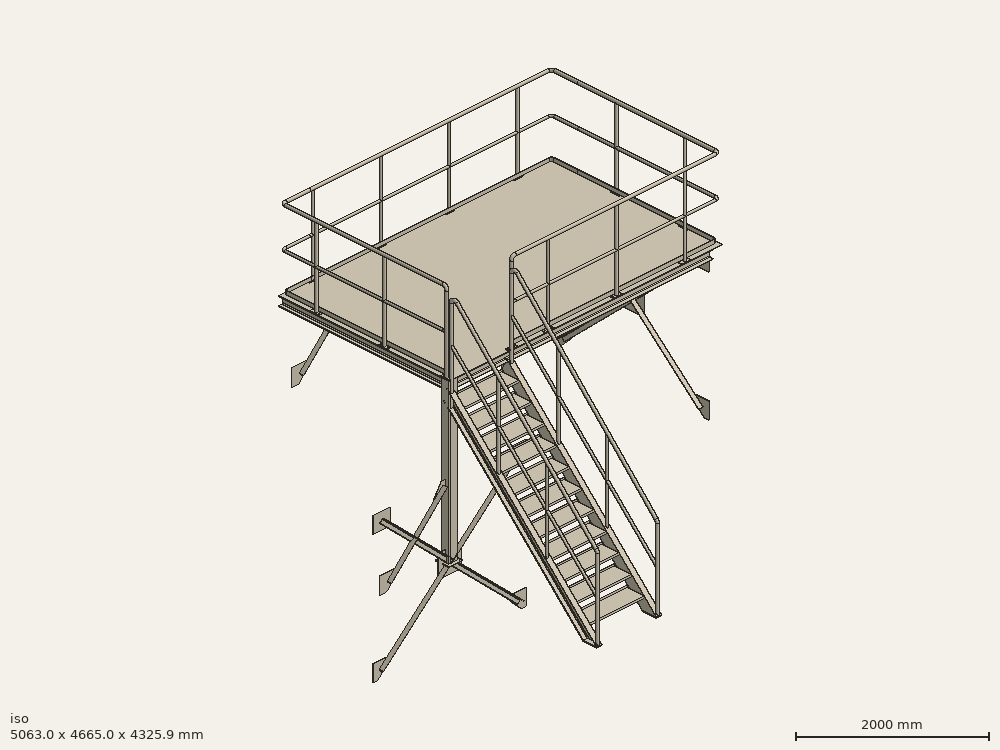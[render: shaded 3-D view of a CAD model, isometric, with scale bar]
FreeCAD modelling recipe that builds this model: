
FCSTD DOCUMENT  (FreeCAD 0.21R33668 +26 (Git))
Label: STBsample
License: All rights reserved
LicenseURL: http://en.wikipedia.org/wiki/All_rights_reserved
objects: Part::FeaturePython×14, Part::Mirroring×6, Part::Extrusion×5, Sketcher::SketchObject×4, Part::MultiFuse×3, Spreadsheet::Sheet×3, App::Part×3, Part::Cut×1
note: 30 computed .brp shape members not serialized (recipe doc carries the construction recipe); baked Part::Feature solids carry a one-line shape summary decoded from their .brp

FEATURE [Part::FeaturePython] BasePlate  # WARN: FeaturePython — macro-defined, semantics opaque (R4)
  B = 200
  D = 15
  H = 200
  b1 = 20
  h1 = 20
  sface = 0
FEATURE [Part::Extrusion] Extrude002  label="Extrude"
  Base = -> BasePlate
  Dir = (0,0,1)
  DirMode = 2
  FaceMakerClass = Part::FaceMakerBullseye
  LengthFwd = 10
  LengthRev = 0
  Solid = true
  Symmetric = false
FEATURE [Part::FeaturePython] Square_Pipe  # WARN: FeaturePython — macro-defined, semantics opaque (R4)
  A = 125
  H = 125
  L = 2200
  Solid = true
  g0 = 7.85
  mass = 47.7221
  size = 40
  standard = SS
  expr: L = Spreadsheet001.H0
FEATURE [Part::MultiFuse] Fusion002  label="PostSq"
  Shapes = -> [Extrude002,Square_Pipe]
FEATURE [Part::FeaturePython] Array  label="post"  # Draft array (typed FeaturePython)
  AlwaysSyncPlacement = false
  Angle = 360
  ArrayType = 0
  Axis = (0,0,1)
  Base = -> Fusion002
  Center = (0,0,0)
  Count = 4
  ExpandArray = false
  Fuse = false
  IntervalAxis = (0,0,0)
  IntervalX = (3875,0,0)
  IntervalY = (0,2375,0)
  IntervalZ = (0,0,2200)
  NumberCircles = 3
  NumberPolar = 5
  NumberX = 2
  NumberY = 2
  NumberZ = 1
  PlacementList = 4 placements: [(0,0,0),(0,2375,0),(3875,0,0),(3875,2375,0)]
  RadialDistance = 50
  ScaleList = (4) [(1,1,1),(1,1,1),(1,1,1),(1,1,1)]
  Symmetry = 1
  TangentialDistance = 25
  expr: .IntervalX.x = Spreadsheet001.W0 - 125
  expr: .IntervalY.y = Spreadsheet001.L0 - 125
FEATURE [Part::FeaturePython] HShapeSteel  # WARN: FeaturePython — macro-defined, semantics opaque (R4)
  B = 125
  H = 125
  L = 2375
  Placement = pos=(0,62.5,2137.5) rot=(-1,0,0;1.5708rad)
  Solid = true
  g0 = 7.85
  mass = 56.5156
  size = 1
  standard = SS_Wide
  t1 = 6.5
  t2 = 9
  expr: .Placement.Base.z = Spreadsheet001.H0 - 62.5
  expr: L = Spreadsheet001.L0 - 125
FEATURE [Part::FeaturePython] Array001  label="beam_v"  # Draft array (typed FeaturePython)
  AlwaysSyncPlacement = false
  Angle = 360
  ArrayType = 0
  Axis = (0,0,1)
  Base = -> HShapeSteel
  Center = (0,0,0)
  Count = 2
  ExpandArray = false
  Fuse = false
  IntervalAxis = (0,0,0)
  IntervalX = (3875,0,0)
  IntervalY = (0,100,0)
  IntervalZ = (0,0,100)
  NumberCircles = 3
  NumberPolar = 5
  NumberX = 2
  NumberY = 1
  NumberZ = 1
  PlacementList = 2 placements: [(0,62.5,2137.5),(3875,62.5,2137.5)]
  RadialDistance = 50
  ScaleList = (2) [(1,1,1),(1,1,1)]
  Symmetry = 1
  TangentialDistance = 25
  expr: .IntervalX.x = Spreadsheet001.W0 - 125
FEATURE [Part::FeaturePython] HShapeSteel001  # WARN: FeaturePython — macro-defined, semantics opaque (R4)
  B = 125
  H = 125
  L = 3750
  Placement = pos=(62.5,0,2137.5) rot=(0.57735,-0.57735,0.57735;4.18879rad)
  Solid = true
  g0 = 7.85
  mass = 89.2351
  size = 1
  standard = SS_Wide
  t1 = 6.5
  t2 = 9
  expr: .Placement.Base.z = Spreadsheet001.H0 - 62.5
  expr: L = Spreadsheet001.W0 - 125 * 2
FEATURE [Part::FeaturePython] Array002  label="beam_h"  # Draft array (typed FeaturePython)
  AlwaysSyncPlacement = false
  Angle = 360
  ArrayType = 0
  Axis = (0,0,1)
  Base = -> HShapeSteel001
  Center = (0,0,0)
  Count = 2
  ExpandArray = false
  Fuse = false
  IntervalAxis = (0,0,0)
  IntervalX = (100,0,0)
  IntervalY = (0,2375,0)
  IntervalZ = (0,0,100)
  NumberCircles = 3
  NumberPolar = 5
  NumberX = 1
  NumberY = 2
  NumberZ = 1
  PlacementList = 2 placements: [(62.5,0,2137.5),(62.5,2375,2137.5)]
  RadialDistance = 50
  ScaleList = (2) [(1,1,1),(1,1,1)]
  Symmetry = 1
  TangentialDistance = 25
  expr: .IntervalY.y = Spreadsheet001.L0 - 125
FEATURE [Spreadsheet::Sheet] Spreadsheet001  label="Spreadsheet"
  cells = A2='W; B2(W0)=4000; A3='L; B3(L0)=2500; A4='H; B4(H0)=2200
FEATURE [Sketcher::SketchObject] Sketch002
  FullyConstrained = true
  expr: Constraints[8] = Spreadsheet001.L0
  expr: Constraints[9] = Spreadsheet001.W0
  sketch-geometry (4):
    g0: LineSegment StartX=-62.5 StartY=-62.5 StartZ=0 EndX=3937.5 EndY=-62.5 EndZ=0
    g1: LineSegment StartX=3937.5 StartY=-62.5 StartZ=0 EndX=3937.5 EndY=2437.5 EndZ=0
    g2: LineSegment StartX=3937.5 StartY=2437.5 StartZ=0 EndX=-62.5 EndY=2437.5 EndZ=0
    g3: LineSegment StartX=-62.5 StartY=2437.5 StartZ=0 EndX=-62.5 EndY=-62.5 EndZ=0
  constraints (12):
    c: Coincident(g0,g1)
    c: Coincident(g1,g2)
    c: Coincident(g2,g3)
    c: Coincident(g3,g0)
    c: Horizontal(g0)
    c: Horizontal(g2)
    c: Vertical(g1)
    c: Vertical(g3)
    c: DistanceY(g3,g3) = 2500
    c: DistanceX(g2,g2) = 4000
    c: DistanceY(g0,g-1) = 62.5
    c: DistanceX(g0,g-1) = 62.5
FEATURE [Part::Extrusion] Extrude003  label="chpl"
  Base = -> Sketch002
  Dir = (0,0,1)
  DirMode = 2
  FaceMakerClass = Part::FaceMakerBullseye
  LengthFwd = 4.5
  LengthRev = 0
  Placement = pos=(0,0,2200) rot=(0,0,1;0rad)
  Solid = true
  Symmetric = false
  expr: .Placement.Base.z = Spreadsheet001.H0
FEATURE [Part::FeaturePython] Corner001  # WARN: FeaturePython — macro-defined, semantics opaque (R4)
  Placement = pos=(363,2413,2204.5) rot=(0,0,1;0rad)
  Reverse = true
  g0 = 7.85
  h = 1100
  k = -90
  l1 = 3550
  l2 = 400
  mass = 43.6699
  p = 1000
  spec = 0
  type = 2
  expr: .Placement.Base.y = Spreadsheet001.L0 - 87
  expr: .Placement.Base.z = Spreadsheet001.H0 + 4.5
  expr: l1 = Spreadsheet001.W0 - 450
FEATURE [Part::FeaturePython] Corner_with_end001  # WARN: FeaturePython — macro-defined, semantics opaque (R4)
  Placement = pos=(877,-37,2204.5) rot=(0,0,1;0rad)
  Reverse = false
  g0 = 7.85
  h = 1100
  k = 90
  l1 = 3036
  l2 = 2050
  mass = 59.9755
  p = 1000
  spec = 0
  type = 1
  expr: .Placement.Base.z = Spreadsheet001.H0 + 4.5
  expr: l1 = Spreadsheet001.W0 - 1000 + 36
  expr: l2 = Spreadsheet001.L0 - 450
FEATURE [Part::FeaturePython] SteelStair  # WARN: FeaturePython — macro-defined, semantics opaque (R4)
  H = 2200
  HighPlace = false
  L = 2200
  L1 = 70
  Placement = pos=(12,-2227,-101.5) rot=(0,0,1;1.5708rad)
  Position = 2
  body = 172.99
  handrail = 57.5144
  mass = 230.504
  size = 1
  t = 9
  type = 1
  w = 800
  expr: .Placement.Base.y = -Spreadsheet001.H0 - 27
FEATURE [Part::FeaturePython] Corner_with_end  # WARN: FeaturePython — macro-defined, semantics opaque (R4)
  Placement = pos=(-36,-8e-15,2204.5) rot=(0,0,1;1.5708rad)
  Reverse = true
  g0 = 7.85
  h = 1100
  k = -90
  l1 = 2413
  l2 = 400
  mass = 32.6673
  p = 1000
  spec = 0
  type = 1
  expr: .Placement.Base.z = Spreadsheet001.H0 + 4.5
  expr: l1 = Spreadsheet001.L0 - 100 + 13
FEATURE [App::Part] Part001  label="Trstle"
  Group = -> [HShapeSteel001,Array002,HShapeSteel,Array001,Fusion002,Square_Pipe,BasePlate,Extrude002,Array,Spreadsheet001,Sketch002,Extrude003,Corner001,Corner_with_end001,SteelStair,Corner_with_end]
  Origin = -> Origin001
FEATURE [Sketcher::SketchObject] Sketch
  FullyConstrained = true
  MapMode = 5
  Placement = pos=(0,0,0) rot=(1,0,0;1.5708rad)
  expr: Constraints[10] = Spreadsheet.H0
  expr: Constraints[11] = Spreadsheet.W0
  expr: Constraints[27] = Spreadsheet.La
  expr: Constraints[28] = Spreadsheet.B0 + 10
  expr: Constraints[37] = Spreadsheet.La
  expr: Constraints[38] = Spreadsheet.B0 + 10
  expr: Constraints[56] = Spreadsheet.B0 + 10
  expr: Constraints[57] = Spreadsheet.La
  expr: Constraints[59] = Spreadsheet.B0 + 10
  expr: Constraints[61] = Spreadsheet.La
  sketch-geometry (36):
    g0: LineSegment StartX=-1125 StartY=-1000 StartZ=0 EndX=-1125 EndY=1000 EndZ=0
    g1: LineSegment StartX=-1125 StartY=1000 StartZ=0 EndX=1125 EndY=1000 EndZ=0
    g2: LineSegment StartX=1125 StartY=1000 StartZ=0 EndX=1125 EndY=-1000 EndZ=0
    g3: LineSegment StartX=1125 StartY=-1000 StartZ=0 EndX=-1125 EndY=-1000 EndZ=0
    g4: GeomPoint X=0 Y=0 Z=0
    g5: LineSegment StartX=-1125 StartY=-1000 StartZ=0 EndX=1125 EndY=1000 EndZ=0
    g6: LineSegment StartX=-1125 StartY=1000 StartZ=0 EndX=1125 EndY=-1000 EndZ=0
    g7: LineSegment StartX=-1125 StartY=1000 StartZ=0 EndX=-875.864 EndY=1000 EndZ=0
    g8: LineSegment StartX=-875.864 StartY=1000 StartZ=0 EndX=-875.864 EndY=828.719 EndZ=0
    g9: LineSegment StartX=-875.864 StartY=828.719 StartZ=0 EndX=-925.691 EndY=772.663 EndZ=0
    g10: LineSegment StartX=-925.691 StartY=772.663 StartZ=0 EndX=-1125 EndY=772.663 EndZ=0
    g11: LineSegment StartX=-1125 StartY=772.663 StartZ=0 EndX=-1125 EndY=1000 EndZ=0
    g12: LineSegment StartX=-1125 StartY=-1000 StartZ=0 EndX=-1050 EndY=-1000 EndZ=0
    g13: LineSegment StartX=-925.691 StartY=-772.663 StartZ=0 EndX=-1125 EndY=-772.663 EndZ=0
    g14: LineSegment StartX=-1125 StartY=-772.663 StartZ=0 EndX=-1125 EndY=-1000 EndZ=0
    g15: LineSegment StartX=-875.864 StartY=-828.719 StartZ=0 EndX=-925.691 EndY=-772.663 EndZ=0
    g16: LineSegment StartX=1125 StartY=1000 StartZ=0 EndX=875.864 EndY=1000 EndZ=0
    g17: LineSegment StartX=875.864 StartY=1000 StartZ=0 EndX=875.864 EndY=828.719 EndZ=0
    g18: LineSegment StartX=925.691 StartY=772.663 StartZ=0 EndX=1125 EndY=772.663 EndZ=0
    g19: LineSegment StartX=1125 StartY=772.663 StartZ=0 EndX=1125 EndY=1000 EndZ=0
    g20: LineSegment StartX=1125 StartY=-1000 StartZ=0 EndX=1050 EndY=-1000 EndZ=0
    g21: LineSegment StartX=925.691 StartY=-772.663 StartZ=0 EndX=1125 EndY=-772.663 EndZ=0
    g22: LineSegment StartX=1125 StartY=-772.663 StartZ=0 EndX=1125 EndY=-1000 EndZ=0
    g23: LineSegment StartX=925.691 StartY=772.663 StartZ=0 EndX=875.864 EndY=828.719 EndZ=0
    g24: LineSegment StartX=875.864 StartY=-828.719 StartZ=0 EndX=925.691 EndY=-772.663 EndZ=0
    g25: LineSegment StartX=-171.074 StartY=-108.582 StartZ=0 EndX=-171.074 EndY=108.582 EndZ=0
    g26: LineSegment StartX=-127.89 StartY=157.164 StartZ=0 EndX=127.89 EndY=157.164 EndZ=0
    g27: LineSegment StartX=171.074 StartY=108.582 StartZ=0 EndX=171.074 EndY=-108.582 EndZ=0
    g28: LineSegment StartX=127.89 StartY=-157.164 StartZ=0 EndX=-127.89 EndY=-157.164 EndZ=0
    g29: GeomPoint X=0 Y=0 Z=0
    g30: LineSegment StartX=171.074 StartY=108.582 StartZ=0 EndX=127.89 EndY=157.164 EndZ=0
    g31: LineSegment StartX=-127.89 StartY=157.164 StartZ=0 EndX=-171.074 EndY=108.582 EndZ=0
    g32: LineSegment StartX=-127.89 StartY=-157.164 StartZ=0 EndX=-171.074 EndY=-108.582 EndZ=0
    g33: LineSegment StartX=127.89 StartY=-157.164 StartZ=0 EndX=171.074 EndY=-108.582 EndZ=0
    g34: LineSegment StartX=-875.864 StartY=-828.719 StartZ=0 EndX=-1050 EndY=-1000 EndZ=0
    g35: LineSegment StartX=875.864 StartY=-828.719 StartZ=0 EndX=1050 EndY=-1000 EndZ=0
  constraints (90):
    c: Coincident(g0,g1)
    c: Coincident(g1,g2)
    c: Coincident(g2,g3)
    c: Coincident(g3,g0)
    c: Horizontal(g1)
    c: Horizontal(g3)
    c: Vertical(g0)
    c: Vertical(g2)
    c: Symmetric(g1,g0,g4)
    c: Coincident(g4,g-1)
    c: DistanceY(g2,g2) = 2000
    c: DistanceX(g1,g1) = 2250
    c: Coincident(g5,g0)
    c: Coincident(g5,g1)
    c: Coincident(g6,g0)
    c: Coincident(g6,g2)
    c: Coincident(g0,g7)
    c: PointOnObject(g7,g1)
    c: Coincident(g7,g8)
    c: Vertical(g8)
    c: Coincident(g8,g9)
    c: Coincident(g9,g10)
    c: PointOnObject(g10,g0)
    c: Horizontal(g10)
    c: Coincident(g10,g11)
    c: Coincident(g11,g7)
    c: Symmetric(g8,g9,g6)
    c: Distance(g7,g9) = 300
    c: Distance(g9) = 75
    c: Coincident(g13,g14)
    c: Coincident(g14,g12)
    c: Horizontal(g12)
    c: Horizontal(g13)
    c: Vertical(g14)
    c: Coincident(g12,g0)
    c: Coincident(g13,g15)
    c: Symmetric(g15,g13,g5)
    c: Distance(g12,g15) = 300
    c: Distance(g15) = 75
    c: Coincident(g16,g17)
    c: Coincident(g18,g19)
    c: Coincident(g19,g16)
    c: Horizontal(g16)
    c: Horizontal(g18)
    c: Vertical(g17)
    c: Vertical(g19)
    c: Coincident(g16,g1)
    c: Coincident(g21,g22)
    c: Coincident(g22,g20)
    c: Horizontal(g20)
    c: Horizontal(g21)
    c: Vertical(g22)
    c: Coincident(g20,g2)
    c: Coincident(g18,g23)
    c: Coincident(g17,g23)
    c: Symmetric(g18,g17,g5)
    c: Distance(g23) = 75
    c: Distance(g16,g23) = 300
    c: Coincident(g21,g24)
    c: Distance(g24) = 75
    c: Symmetric(g21,g24,g6)
    c: Distance(g20,g24) = 300
    c: Horizontal(g26)
    c: Horizontal(g28)
    c: Vertical(g25)
    c: Vertical(g27)
    c: Coincident(g29,g4)
    c: Coincident(g27,g30)
    c: Coincident(g26,g30)
    c: Coincident(g26,g31)
    c: Coincident(g25,g31)
    c: Coincident(g25,g32)
    c: Coincident(g28,g32)
    c: Coincident(g28,g33)
    c: Coincident(g27,g33)
    c: Perpendicular(g5,g32)
    c: Distance(g31) = 65
    c: Symmetric(g26,g25,g6)
    c: Equal(g31,g30)
    c: Equal(g33,g31)
    c: Equal(g31,g32)
    c: Symmetric(g27,g26,g5)
    c: Symmetric(g27,g28,g6)
    c: Distance(g4,g30) = 200
    c: Coincident(g12,g34)
    c: DistanceX(g12,g12) = 75
    c: Coincident(g34,g15)
    c: Coincident(g20,g35)
    c: DistanceX(g20,g20) = 75
    c: Coincident(g35,g24)
FEATURE [Part::Extrusion] Extrude  label="GPL"
  Base = -> Sketch
  Dir = (0,-1,2e-16)
  DirMode = 2
  FaceMakerClass = Part::FaceMakerBullseye
  LengthFwd = 6
  LengthRev = 0
  Solid = true
  Symmetric = false
FEATURE [Spreadsheet::Sheet] Spreadsheet  label="STB02"
  cells = A2='ブレース幅W0; B2(W0)=2250; A3='ブレース高H0; B3(H0)=2000; A4='ブレース長C0; B4(C0)==sqrt(W0 ^ 2 + H0 ^ 2); A5='ガセットプレートLa; B5(La)=300; A6='ブレース角度k0; B6(k0)==atan(H0 / W0); A7='ブレース部材幅B0; B7(B0)=65
FEATURE [Part::FeaturePython] AngleSteel  # WARN: FeaturePython — macro-defined, semantics opaque (R4)
  A = 65
  B = 65
  L = 1355.2
  Placement = pos=(0,-38.5,0) rot=(0,1,0;2.29744rad)
  Solid = true
  g0 = 7.85
  mass = 8.0068
  sface = 0
  size = 8
  standard = SS_Equal
  t = 6
  expr: .Placement.Rotation.Angle = Spreadsheet.k0 + 90 °
  expr: L = Spreadsheet.C0 / 2 - Spreadsheet.La + 150
FEATURE [Part::Mirroring] Part__Mirroring001  label="AngleSteel (Mirror #2)"
  Base = (0,0,0)
  Normal = (1,0,0)
  Placement = pos=(0,-8,0) rot=(0,1,0;1.45328rad)
  Source = -> AngleSteel
  expr: .Placement.Rotation.Angle = Spreadsheet.k0 * 2
FEATURE [Part::FeaturePython] AngleSteel001  # WARN: FeaturePython — macro-defined, semantics opaque (R4)
  A = 65
  B = 65
  L = 1355.2
  Placement = pos=(0,-38.5,0) rot=(0,1,0;0.844154rad)
  Solid = true
  g0 = 7.85
  mass = 8.0068
  sface = 1
  size = 8
  standard = SS_Equal
  t = 6
  expr: .Placement.Rotation.Angle = 90 ° - Spreadsheet.k0
  expr: L = Spreadsheet.C0 / 2 - Spreadsheet.La + 150
FEATURE [Part::Mirroring] Part__Mirroring  label="AngleSteel001 (Mirror #2)"
  Base = (0,0,0)
  Normal = (0,0,1)
  Placement = pos=(0,0,0) rot=(0,1,0;1.68831rad)
  Source = -> AngleSteel001
  expr: .Placement.Rotation.Angle = (90 ° - Spreadsheet.k0) * 2
FEATURE [Part::MultiFuse] Fusion  label="beam_b"
  Refine = true
  Shapes = -> [Part__Mirroring001,AngleSteel]
FEATURE [Part::MultiFuse] Fusion001  label="beamA"
  Shapes = -> [Part__Mirroring,AngleSteel001]
FEATURE [Sketcher::SketchObject] Sketch001
  ExternalGeometry = -> [Extrude,Fusion001,Fusion]
  FullyConstrained = true
  MapMode = 5
  Placement = pos=(0,-6,1.3e-15) rot=(1,0,0;1.5708rad)
  Support = -> [Extrude]
  sketch-geometry (4):
    g0: LineSegment StartX=0 StartY=69.5737 StartZ=0 EndX=-78.2704 EndY=0 EndZ=0
    g1: LineSegment StartX=-78.2704 StartY=0 StartZ=0 EndX=-2.84e-14 EndY=-69.5737 EndZ=0
    g2: LineSegment StartX=-3.11e-14 StartY=-69.5737 StartZ=0 EndX=78.2704 EndY=0 EndZ=0
    g3: LineSegment StartX=78.2704 StartY=0 StartZ=0 EndX=0 EndY=69.5737 EndZ=0
  constraints (12):
    c: PointOnObject(g0,g-2)
    c: PointOnObject(g0,g-1)
    c: Coincident(g0,g1)
    c: Coincident(g1,g2)
    c: PointOnObject(g2,g-1)
    c: Coincident(g2,g3)
    c: Coincident(g3,g0)
    c: Parallel(g-4,g0)
    c: Parallel(g0,g2)
    c: Parallel(g-5,g3)
    c: Parallel(g3,g1)
    c: Distance(g-1,g0) = 52
FEATURE [Part::Extrusion] Extrude001
  Base = -> Sketch001
  Dir = (0,-1,2e-16)
  DirMode = 2
  FaceMakerClass = Part::FaceMakerBullseye
  LengthFwd = 100
  LengthRev = 0
  Solid = true
  Symmetric = false
FEATURE [Part::Cut] Cut  label="beamB"
  Base = -> Fusion
  Tool = -> Extrude001
FEATURE [App::Part] Part  label="steelBrace02"
  Group = -> [Fusion,Fusion001,Sketch001,Part__Mirroring,Sketch,Part__Mirroring001,Extrude,Extrude001,AngleSteel001,AngleSteel,Cut,Spreadsheet]
  Origin = -> Origin
  Placement = pos=(-3.62,1186.97,1074) rot=(0,0,-1;4.71239rad)
FEATURE [Part::Mirroring] Mirror  label="steelBrace02 (mirrored)"
  Base = (1600,3000,0)
  Normal = (1,0,0)
  Placement = pos=(675,0,0) rot=(0,0,1;0rad)
  Source = -> Part
FEATURE [Sketcher::SketchObject] Sketch003
  FullyConstrained = true
  MapMode = 5
  Placement = pos=(0,0,0) rot=(1,0,0;1.5708rad)
  expr: Constraints[10] = Spreadsheet002.H0
  expr: Constraints[12] = Spreadsheet002.B0 + 10
  expr: Constraints[26] = Spreadsheet002.Lc
  expr: Constraints[30] = Spreadsheet002.W0
  expr: Constraints[32] = Spreadsheet002.La
  expr: Constraints[33] = Spreadsheet002.B0 + 10
  expr: Constraints[38] = Spreadsheet002.La
  sketch-geometry (16):
    g0: LineSegment StartX=0 StartY=0 StartZ=0 EndX=-1000 EndY=0 EndZ=0
    g1: GeomPoint X=0 Y=0 Z=0
    g2: LineSegment StartX=0 StartY=1000 StartZ=0 EndX=-1000 EndY=0 EndZ=0
    g3: LineSegment StartX=0 StartY=1000 StartZ=0 EndX=-120 EndY=1000 EndZ=0
    g4: LineSegment StartX=-120 StartY=1000 StartZ=0 EndX=-238.649 EndY=814.384 EndZ=0
    g5: LineSegment StartX=-1000 StartY=0 StartZ=0 EndX=-925 EndY=0 EndZ=0
    g6: LineSegment StartX=-814.384 StartY=238.649 StartZ=0 EndX=-1000 EndY=238.649 EndZ=0
    g7: LineSegment StartX=-185.616 StartY=761.351 StartZ=0 EndX=-238.649 EndY=814.384 EndZ=0
    g8: LineSegment StartX=-814.384 StartY=238.649 StartZ=0 EndX=-761.351 EndY=185.616 EndZ=0
    g9: LineSegment StartX=-761.351 StartY=185.616 StartZ=0 EndX=-925 EndY=0 EndZ=0
    g10: LineSegment StartX=-1000 StartY=0 StartZ=0 EndX=-1030 EndY=0 EndZ=0
    g11: LineSegment StartX=-1030 StartY=0 StartZ=0 EndX=-1030 EndY=238.649 EndZ=0
    g12: LineSegment StartX=-1000 StartY=238.649 StartZ=0 EndX=-1030 EndY=238.649 EndZ=0
    g13: LineSegment StartX=0 StartY=0 StartZ=0 EndX=0 EndY=1000 EndZ=0
    g14: LineSegment StartX=-185.616 StartY=761.351 StartZ=0 EndX=120 EndY=1000 EndZ=0
    g15: LineSegment StartX=120 StartY=1000 StartZ=0 EndX=0 EndY=1000 EndZ=0
  constraints (42):
    c: Horizontal(g0)
    c: Coincident(g1,g-1)
    c: Coincident(g3,g4)
    c: Horizontal(g3)
    c: Horizontal(g5)
    c: Horizontal(g6)
    c: Coincident(g5,g0)
    c: Coincident(g4,g7)
    c: PointOnObject(g2,g-2)
    c: Coincident(g2,g5)
    c: Distance(g2,g0) = 1000
    c: Symmetric(g7,g4,g2)
    c: Distance(g7) = 75
    c: Coincident(g6,g8)
    c: PointOnObject(g1,g0)
    c: Coincident(g5,g9)
    c: DistanceX(g5,g5) = 75
    c: Coincident(g9,g8)
    c: Coincident(g5,g10)
    c: PointOnObject(g10,g-1)
    c: Coincident(g10,g11)
    c: Vertical(g11)
    c: Vertical(g5,g6)
    c: Coincident(g12,g6)
    c: Coincident(g12,g11)
    c: Horizontal(g12)
    c: DistanceX(g12,g12) = 30
    c: Coincident(g13,g1)
    c: Coincident(g13,g2)
    c: PointOnObject(g0,g13)
    c: DistanceX(g5,g0) = 1000
    c: Symmetric(g8,g6,g2)
    c: Distance(g5,g8) = 300
    c: Distance(g8) = 75
    c: Distance(g3) = 120
    c: Coincident(g15,g14)
    c: Horizontal(g15)
    c: DistanceX(g15,g15) = 120
    c: Distance(g3,g7) = 300
    c: Coincident(g3,g15)
    c: Coincident(g2,g3)
    c: Coincident(g14,g7)
FEATURE [Part::Extrusion] Extrude004  label="steelBrace"
  Base = -> Sketch003
  Dir = (0,-1,2e-16)
  DirMode = 2
  FaceMakerClass = Part::FaceMakerBullseye
  LengthFwd = 6
  LengthRev = 0
  Solid = true
  Symmetric = false
FEATURE [Part::FeaturePython] AngleSteel002  # WARN: FeaturePython — macro-defined, semantics opaque (R4)
  A = 65
  B = 65
  L = 1164.21
  Placement = pos=(-893.934,-38.5,106.066) rot=(0,1,0;0.785398rad)
  Solid = true
  g0 = 7.85
  mass = 6.87841
  sface = 0
  size = 8
  standard = SS_Equal
  t = 6
  expr: .Placement.Base.x = Spreadsheet002.Lx
  expr: .Placement.Base.y = -Spreadsheet002.B0 / 2 - 6
  expr: .Placement.Base.z = Spreadsheet002.Ly
  expr: .Placement.Rotation.Angle = Spreadsheet002.k0
  expr: L = Spreadsheet002.LL - Spreadsheet002.La + 50
FEATURE [Spreadsheet::Sheet] Spreadsheet002  label="STB04"
  cells = A2='W0; B2(W0)=1000; A3='H0; B3(H0)=1000; A4='k0; B4(k0)==90 ° - atan(H0 / W0); A5='La; B5(La)=300; A6='Lb; B6(Lb)==La - 150; A7='LL; B7(LL)==sqrt(W0 ^ 2 + H0 ^ 2); A8='Lc; B8(Lc)=30; A9='Lx; B9(Lx)==-W0 + Lb * sin(k0); A10='Ly; B10(Ly)==Lb * cos(k0); A11='B0; B11(B0)=65
FEATURE [App::Part] Part002  label="steelBrace04"
  Group = -> [AngleSteel002,Spreadsheet002,Sketch003,Extrude004]
  Origin = -> Origin002
  Placement = pos=(2787,-3,1074) rot=(0,0,1;3.14159rad)
FEATURE [Part::Mirroring] Mirror001  label="steelBrace04 (mirrored)"
  Base = (3787,-5.146e-13,1312.65)
  Normal = (-1,0,0)
  Placement = pos=(-3694,0,0) rot=(0,0,1;0rad)
  Source = -> Part002
FEATURE [Part::Mirroring] Mirror002  label="steelBrace04 (mirrored) (mirrored)"
  Base = (0,1200,1300)
  Normal = (0,-1,0)
  Placement = pos=(0,-23,0) rot=(0,0,1;0rad)
  Source = -> Mirror001
FEATURE [Part::Mirroring] Mirror003  label="steelBrace04 (mirrored)001"
  Base = (0,1200,1300)
  Normal = (0,-1,0)
  Placement = pos=(0,-23,0) rot=(0,0,1;0rad)
  Source = -> Part002
